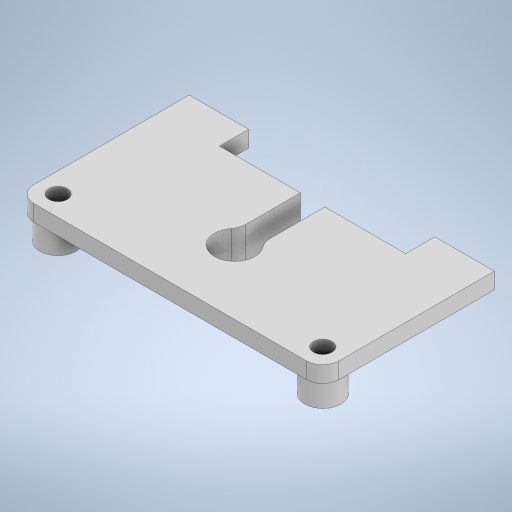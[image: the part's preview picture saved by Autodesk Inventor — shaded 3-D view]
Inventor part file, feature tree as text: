
AUTODESK INVENTOR PART (.ipt)
format: ipt  version: 2024.2 (Build 282272000, 272)  size: 384,000 bytes
history: native  units: mm
features: sketch x13, extrude x12, fillet x2
ambient origin geometry x8: Origin, YZ Plane, XZ Plane, XY Plane, X Axis, Y Axis, Z Axis, Center Point
bodies: Solid1 (feature_tree)
feature tree (27):
  extrude  "Extrusion1"  Depth=28.0mm
  extrude  "Extrusion2"  Depth=3.0mm
  extrude  "Extrusion3"  Depth=4.0mm
  extrude  "Extrusion4"  Depth=3.0mm TaperAngle=0.0deg
  fillet  "Fillet1"  Radius=48.2mm
  extrude  "Extrusion6"  Depth=4.85mm
  extrude  "Extrusion9"  Depth=2.0mm TaperAngle=0.0deg
  extrude  "Extrusion11"  Depth=2.35mm
  extrude  "Extrusion12"  Depth=4.5mm
  extrude  "Extrusion13"  Depth=2.35mm
  fillet  "Fillet3"  Radius=4.5mm
  sketch  "Sketch12"  dims[d27=2.35mm d28=4.5mm]
  extrude  "Extrusion14"  Depth=4.5mm
  extrude  "Extrusion16"  Depth=2.35mm
  extrude  "Extrusion17"  Depth=3.0mm TaperAngle=0.0deg
  sketch  "Sketch1"  dims[d0=28.0mm d1=38.5mm]
  sketch  "Sketch2"  dims[d6=3.0mm d7=0.0mm d8=4.0mm]
  sketch  "Sketch3"  dims[d9=4.0mm d10=4.0mm]
  sketch  "Sketch4"  dims[d11=4.0mm d12=3.0mm d13=0.0mm d14=48.2mm]
  sketch  "Sketch5"  dims[d15=37.7mm d16=4.85mm]
  sketch  "Sketch8"  dims[d17=4.85mm d18=2.0mm d19=0.0mm]
  sketch  "Sketch9"  dims[d20=4.5mm d21=2.35mm]
  sketch  "Sketch10"  dims[d22=2.35mm d23=4.5mm]
  sketch  "Sketch11"  dims[d24=2.35mm d25=2.35mm d26=4.5mm]
  sketch  "Sketch13"  dims[d29=2.35mm d30=2.35mm]
  sketch  "Sketch15"  dims[d31=2.35mm d32=3.0mm d33=0.0mm]
  sketch  "Sketch16"  dims[d34=2.0mm d45=2.0mm d46=2.0mm d51=0.0mm d52=0.0mm d68=5.0mm d69=3.125mm d70=18.85mm d71=0.0mm d72=0.0mm d73=28.0mm d76=3.0mm d77=1.5mm d81=24.1mm d82=4.85mm d83=23.0mm d84=13.0mm d85=7.35mm d86=6.5mm d87=0.0mm d88=0.0mm d90=0.0mm d91=0.0mm d93=0.0mm d94=0.0mm d95=2.0mm d96=2.3mm d97=2.3mm d98=0.0mm d99=0.0mm d107=4.0mm d108=0.0mm d109=2.5mm d110=2.5mm d111=0.4mm d112=0.0mm d113=0.0mm d63=0.5mm d64=0.872665mm d65=0.5mm d66=0.872665mm]
